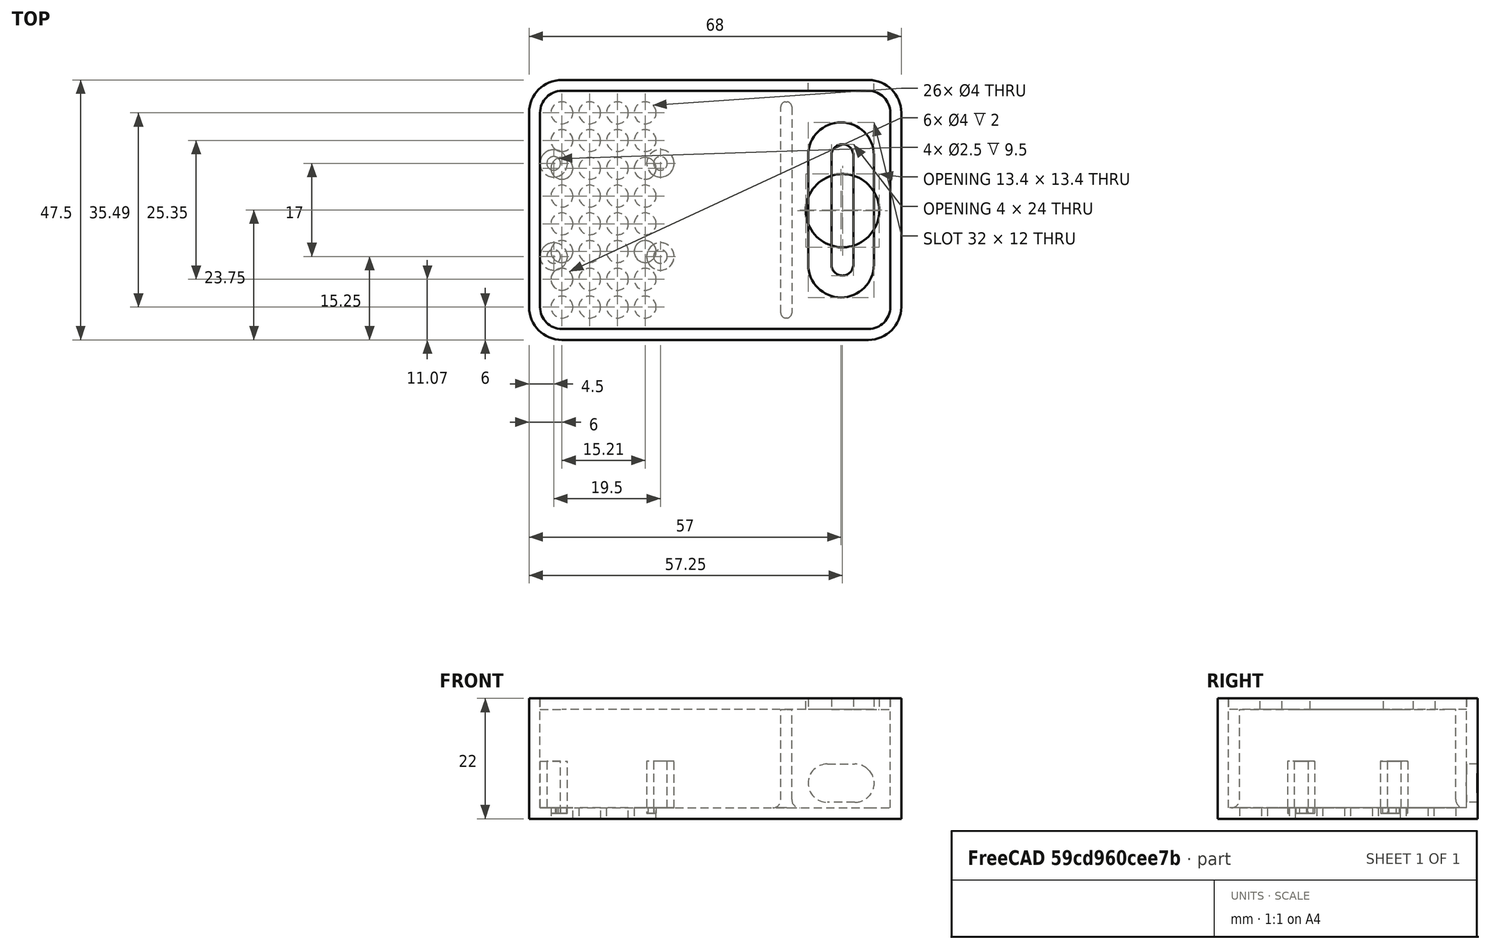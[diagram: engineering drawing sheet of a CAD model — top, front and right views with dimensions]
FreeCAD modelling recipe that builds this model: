
FCSTD DOCUMENT  (FreeCAD 0.20R29410 (Git))
Label: co2-sensor-case-v2
License: All rights reserved
LicenseURL: http://en.wikipedia.org/wiki/All_rights_reserved
objects: Sketcher::SketchObject×10, Part::Extrusion×5, PartDesign::Body×5, PartDesign::FeatureBase×4, Part::Fillet×3, PartDesign::Pocket×3, Part::Fuse×2, PartDesign::Thickness×1, Part::Cut×1
note: 38 computed .brp shape members not serialized (recipe doc carries the construction recipe); baked Part::Feature solids carry a one-line shape summary decoded from their .brp

FEATURE [Sketcher::SketchObject] Sketch
  FullyConstrained = true
  sketch-geometry (4):
    g0: LineSegment StartX=-34 StartY=23.75 StartZ=0 EndX=34 EndY=23.75 EndZ=0
    g1: LineSegment StartX=34 StartY=23.75 StartZ=0 EndX=34 EndY=-23.75 EndZ=0
    g2: LineSegment StartX=34 StartY=-23.75 StartZ=0 EndX=-34 EndY=-23.75 EndZ=0
    g3: LineSegment StartX=-34 StartY=-23.75 StartZ=0 EndX=-34 EndY=23.75 EndZ=0
  constraints (12):
    c: Coincident(g0,g1)
    c: Coincident(g1,g2)
    c: Coincident(g2,g3)
    c: Coincident(g3,g0)
    c: Horizontal(g0)
    c: Horizontal(g2)
    c: Vertical(g1)
    c: Vertical(g3)
    c: DistanceX(g0,g0) = 68
    c: DistanceY(g1,g1) = 47.5
    c: DistanceX(g-1,g0) = 34
    c: DistanceY(g-1,g0) = 23.75
FEATURE [Part::Extrusion] Extrude
  Base = -> Sketch
  Dir = (0,0,1)
  DirMode = 2
  FaceMakerClass = Part::FaceMakerBullseye
  LengthFwd = 22
  LengthRev = 0
  Solid = true
  Symmetric = false
FEATURE [Part::Fillet] Fillet
  Base = -> Extrude
  Edges = 4 edges r=6: [Edge1,Edge2,Edge5,Edge8]
FEATURE [PartDesign::FeatureBase] BaseFeature
  BaseFeature = -> Fillet
FEATURE [PartDesign::Thickness] Thickness
  Base = -> BaseFeature [Face5]
  BaseFeature = -> BaseFeature
  Intersection = false
  Join = 0
  Mode = 0
  Reversed = true
  SupportTransform = false
  Value = 2
FEATURE [Sketcher::SketchObject] Sketch001
  ExternalGeometry = -> [Thickness]
  FullyConstrained = true
  MapMode = 5
  Placement = pos=(0,0,2) rot=(0,0,1;0rad)
  Support = -> [Thickness]
  sketch-geometry (12):
    g0: Circle CenterX=-29.5 CenterY=8.5 CenterZ=0 NormalX=0 NormalY=0 NormalZ=1 AngleXU=0 Radius=2.5
    g1: Circle CenterX=-29.5 CenterY=8.5 CenterZ=0 NormalX=0 NormalY=0 NormalZ=1 AngleXU=0 Radius=1.25
    g2: Circle CenterX=-10 CenterY=8.5 CenterZ=0 NormalX=0 NormalY=0 NormalZ=1 AngleXU=0 Radius=1.25
    g3: Circle CenterX=-10 CenterY=8.5 CenterZ=0 NormalX=0 NormalY=0 NormalZ=1 AngleXU=0 Radius=2.5
    g4: Circle CenterX=-29.5 CenterY=-8.5 CenterZ=0 NormalX=0 NormalY=0 NormalZ=1 AngleXU=0 Radius=1.25
    g5: Circle CenterX=-29.5 CenterY=-8.5 CenterZ=0 NormalX=0 NormalY=0 NormalZ=1 AngleXU=0 Radius=2.5
    g6: Circle CenterX=-10 CenterY=-8.5 CenterZ=0 NormalX=0 NormalY=0 NormalZ=1 AngleXU=0 Radius=1.25
    g7: Circle CenterX=-10 CenterY=-8.5 CenterZ=0 NormalX=0 NormalY=0 NormalZ=1 AngleXU=0 Radius=2.5
    g8: LineSegment StartX=12 StartY=19.75 StartZ=0 EndX=14 EndY=19.75 EndZ=0
    g9: LineSegment StartX=14 StartY=19.75 StartZ=0 EndX=14 EndY=-19.75 EndZ=0
    g10: LineSegment StartX=14 StartY=-19.75 StartZ=0 EndX=12 EndY=-19.75 EndZ=0
    g11: LineSegment StartX=12 StartY=-19.75 StartZ=0 EndX=12 EndY=19.75 EndZ=0
  constraints (32):
    c: Coincident(g1,g0)
    c: Diameter(g0) = 5
    c: Diameter(g1) = 2.5
    c: Coincident(g2,g3)
    c: Equal(g0,g3) = 5
    c: Equal(g1,g2) = 2.5
    c: DistanceX(g0,g2) = 19.5
    c: DistanceY(g2,g0) = 0
    c: Coincident(g4,g5)
    c: Equal(g0,g5) = 5
    c: Equal(g1,g4) = 2.5
    c: Coincident(g6,g7)
    c: Equal(g5,g7) = 5
    c: Equal(g4,g6) = 2.5
    c: DistanceX(g5,g6) = 19.5
    c: DistanceY(g6,g5) = 0
    c: DistanceX(g2,g6) = 0
    c: DistanceY(g6,g2) = 17
    c: DistanceY(g-1,g2) = 8.5
    c: DistanceX(g-7,g0) = 2.5
    c: Coincident(g8,g9)
    c: Coincident(g9,g10)
    c: Coincident(g10,g11)
    c: Coincident(g11,g8)
    c: Horizontal(g8)
    c: Horizontal(g10)
    c: Vertical(g9)
    c: Vertical(g11)
    c: DistanceX(g8,g8) = 2
    c: DistanceY(g9,g9) = 39.5
    c: DistanceX(g8,g-10) = 18
    c: DistanceY(g-1,g8) = 19.75
FEATURE [Part::Extrusion] Extrude001
  Base = -> Sketch001
  Dir = (0,0,1)
  DirMode = 2
  FaceMakerClass = Part::FaceMakerBullseye
  LengthFwd = 8.5
  LengthRev = 1
  Solid = true
  Symmetric = false
FEATURE [Sketcher::SketchObject] Sketch002
  ExternalGeometry = -> [Extrude001]
  FullyConstrained = true
  MapMode = 5
  Placement = pos=(0,0,10.5) rot=(0,0,1;0rad)
  Support = -> [Extrude001]
  sketch-geometry (4):
    g0: LineSegment StartX=12 StartY=19.75 StartZ=0 EndX=14 EndY=19.75 EndZ=0
    g1: LineSegment StartX=14 StartY=19.75 StartZ=0 EndX=14 EndY=-19.75 EndZ=0
    g2: LineSegment StartX=14 StartY=-19.75 StartZ=0 EndX=12 EndY=-19.75 EndZ=0
    g3: LineSegment StartX=12 StartY=-19.75 StartZ=0 EndX=12 EndY=19.75 EndZ=0
  constraints (10):
    c: Coincident(g0,g1)
    c: Coincident(g1,g2)
    c: Coincident(g2,g3)
    c: Coincident(g3,g0)
    c: Horizontal(g0)
    c: Horizontal(g2)
    c: Vertical(g1)
    c: Vertical(g3)
    c: Coincident(g0,g-5)
    c: Coincident(g1,g-6)
FEATURE [Part::Extrusion] Extrude002
  Base = -> Sketch002
  Dir = (0,0,1)
  DirMode = 2
  FaceMakerClass = Part::FaceMakerBullseye
  LengthFwd = 9.5
  LengthRev = 0
  Solid = true
  Symmetric = false
FEATURE [Sketcher::SketchObject] Sketch003
  ExternalGeometry = -> [Thickness]
  FullyConstrained = true
  MapMode = 5
  Placement = pos=(0,0,22) rot=(0,0,1;0rad)
  Support = -> [Thickness]
  sketch-geometry (8):
    g0: LineSegment StartX=-28 StartY=21.75 StartZ=0 EndX=28 EndY=21.75 EndZ=0
    g1: LineSegment StartX=32 StartY=17.75 StartZ=0 EndX=32 EndY=-17.75 EndZ=0
    g2: LineSegment StartX=28 StartY=-21.75 StartZ=0 EndX=-28 EndY=-21.75 EndZ=0
    g3: LineSegment StartX=-32 StartY=-17.75 StartZ=0 EndX=-32 EndY=17.75 EndZ=0
    g4: ArcOfCircle CenterX=-28 CenterY=17.75 CenterZ=0 NormalX=0 NormalY=0 NormalZ=1 AngleXU=0 Radius=4 StartAngle=1.5708 EndAngle=3.14159
    g5: ArcOfCircle CenterX=-28 CenterY=-17.75 CenterZ=0 NormalX=0 NormalY=0 NormalZ=1 AngleXU=0 Radius=4 StartAngle=3.14159 EndAngle=4.71239
    g6: ArcOfCircle CenterX=28 CenterY=-17.75 CenterZ=0 NormalX=0 NormalY=0 NormalZ=1 AngleXU=0 Radius=4 StartAngle=4.71239 EndAngle=6.28319
    g7: ArcOfCircle CenterX=28 CenterY=17.75 CenterZ=0 NormalX=0 NormalY=0 NormalZ=1 AngleXU=0 Radius=4 StartAngle=-9e-16 EndAngle=1.5708
  constraints (20):
    c: Coincident(g0,g-4)
    c: Coincident(g0,g-10)
    c: Coincident(g1,g-10)
    c: Coincident(g1,g-9)
    c: Coincident(g2,g-8)
    c: Coincident(g2,g-7)
    c: Coincident(g3,g-6)
    c: Coincident(g3,g-5)
    c: Coincident(g4,g-3)
    c: Coincident(g4,g0)
    c: Coincident(g4,g3)
    c: Coincident(g5,g-6)
    c: Coincident(g5,g3)
    c: Coincident(g5,g2)
    c: Coincident(g6,g-8)
    c: Coincident(g6,g2)
    c: Coincident(g6,g1)
    c: Coincident(g7,g-10)
    c: Coincident(g7,g0)
    c: Coincident(g7,g1)
FEATURE [Part::Extrusion] Extrude003
  Base = -> Sketch003
  Dir = (0,0,1)
  DirMode = 2
  FaceMakerClass = Part::FaceMakerBullseye
  LengthFwd = 2
  LengthRev = 0
  Reversed = true
  Solid = true
  Symmetric = false
FEATURE [Sketcher::SketchObject] Sketch004
  ExternalGeometry = -> [Thickness]
  FullyConstrained = false
  MapMode = 5
  Placement = pos=(0,0,22) rot=(0,0,1;0rad)
  Support = -> [Extrude003]
  sketch-geometry (5):
    g0: ArcOfCircle CenterX=23.25 CenterY=10 CenterZ=0 NormalX=0 NormalY=0 NormalZ=1 AngleXU=0 Radius=2 StartAngle=4e-16 EndAngle=3.14159
    g1: ArcOfCircle CenterX=23.25 CenterY=-10 CenterZ=0 NormalX=0 NormalY=0 NormalZ=1 AngleXU=0 Radius=2 StartAngle=3.14159 EndAngle=6.28319
    g2: LineSegment StartX=21.25 StartY=10 StartZ=0 EndX=21.25 EndY=-10 EndZ=0
    g3: LineSegment StartX=25.25 StartY=-10 StartZ=0 EndX=25.25 EndY=10 EndZ=0
    g4: Circle CenterX=23.2654 CenterY=-0.133764 CenterZ=0 NormalX=0 NormalY=0 NormalZ=1 AngleXU=0 Radius=6.6979
  constraints (9):
    c: Tangent(g0,g2) = -1.5708
    c: Tangent(g2,g1) = -1.5708
    c: Tangent(g1,g3) = -1.5708
    c: Tangent(g3,g0) = -1.5708
    c: Equal(g0,g1)
    c: Symmetric(g0,g1,g-1)
    c: DistanceY(g-1,g0) = 10
    c: Radius(g0) = 2
    c: DistanceX(g0,g-3) = 6.75
FEATURE [PartDesign::FeatureBase] BaseFeature001
  BaseFeature = -> Extrude003
FEATURE [PartDesign::Pocket] Pocket
  BaseFeature = -> BaseFeature001
  Direction = (0,0,-1)
  Length = 2
  Length2 = 5
  Profile = -> Sketch004
  ReferenceAxis = -> Sketch004 [N_Axis]
  Type = 0
FEATURE [Sketcher::SketchObject] Sketch005
  ExternalGeometry = -> [Thickness]
  FullyConstrained = true
  MapMode = 5
  Placement = pos=(0,0,0) rot=(1,0,0;3.14159rad)
  Support = -> [Thickness]
  sketch-geometry (63):
    g0: Circle CenterX=-28 CenterY=17.75 CenterZ=0 NormalX=0 NormalY=0 NormalZ=1 AngleXU=0 Radius=2
    g1: Circle CenterX=-22.93 CenterY=17.75 CenterZ=0 NormalX=0 NormalY=0 NormalZ=1 AngleXU=0 Radius=2
    g2: LineSegment StartX=-28 StartY=17.75 StartZ=0 EndX=-22.93 EndY=17.75 EndZ=0
    g3: Circle CenterX=-17.86 CenterY=17.75 CenterZ=0 NormalX=0 NormalY=0 NormalZ=1 AngleXU=0 Radius=2
    g4: LineSegment StartX=-22.93 StartY=17.75 StartZ=0 EndX=-17.86 EndY=17.75 EndZ=0
    g5: Circle CenterX=-12.79 CenterY=17.75 CenterZ=0 NormalX=0 NormalY=0 NormalZ=1 AngleXU=0 Radius=2
    g6: LineSegment StartX=-17.86 StartY=17.75 StartZ=0 EndX=-12.79 EndY=17.75 EndZ=0
    g7: Circle CenterX=-28 CenterY=12.68 CenterZ=0 NormalX=0 NormalY=0 NormalZ=1 AngleXU=0 Radius=2
    g8: LineSegment StartX=-28 StartY=17.75 StartZ=0 EndX=-28 EndY=12.68 EndZ=0
    g9: Circle CenterX=-22.93 CenterY=12.68 CenterZ=0 NormalX=0 NormalY=0 NormalZ=1 AngleXU=0 Radius=2
    g10: LineSegment StartX=-28 StartY=12.68 StartZ=0 EndX=-22.93 EndY=12.68 EndZ=0
    g11: Circle CenterX=-17.86 CenterY=12.68 CenterZ=0 NormalX=0 NormalY=0 NormalZ=1 AngleXU=0 Radius=2
    g12: LineSegment StartX=-22.93 StartY=12.68 StartZ=0 EndX=-17.86 EndY=12.68 EndZ=0
    g13: Circle CenterX=-12.79 CenterY=12.68 CenterZ=0 NormalX=0 NormalY=0 NormalZ=1 AngleXU=0 Radius=2
    g14: LineSegment StartX=-17.86 StartY=12.68 StartZ=0 EndX=-12.79 EndY=12.68 EndZ=0
    g15: Circle CenterX=-28 CenterY=7.61 CenterZ=0 NormalX=0 NormalY=0 NormalZ=1 AngleXU=0 Radius=2
    g16: LineSegment StartX=-28 StartY=12.68 StartZ=0 EndX=-28 EndY=7.61 EndZ=0
    g17: Circle CenterX=-22.93 CenterY=7.61 CenterZ=0 NormalX=0 NormalY=0 NormalZ=1 AngleXU=0 Radius=2
    g18: LineSegment StartX=-28 StartY=7.61 StartZ=0 EndX=-22.93 EndY=7.61 EndZ=0
    g19: Circle CenterX=-17.86 CenterY=7.61 CenterZ=0 NormalX=0 NormalY=0 NormalZ=1 AngleXU=0 Radius=2
    g20: LineSegment StartX=-22.93 StartY=7.61 StartZ=0 EndX=-17.86 EndY=7.61 EndZ=0
    g21: Circle CenterX=-12.79 CenterY=7.61 CenterZ=0 NormalX=0 NormalY=0 NormalZ=1 AngleXU=0 Radius=2
    g22: LineSegment StartX=-17.86 StartY=7.61 StartZ=0 EndX=-12.79 EndY=7.61 EndZ=0
    g23: Circle CenterX=-28 CenterY=2.54 CenterZ=0 NormalX=0 NormalY=0 NormalZ=1 AngleXU=0 Radius=2
    g24: LineSegment StartX=-28 StartY=7.61 StartZ=0 EndX=-28 EndY=2.54 EndZ=0
    g25: Circle CenterX=-22.93 CenterY=2.54 CenterZ=0 NormalX=0 NormalY=0 NormalZ=1 AngleXU=0 Radius=2
    g26: LineSegment StartX=-28 StartY=2.54 StartZ=0 EndX=-22.93 EndY=2.54 EndZ=0
    g27: Circle CenterX=-17.86 CenterY=2.54 CenterZ=0 NormalX=0 NormalY=0 NormalZ=1 AngleXU=0 Radius=2
    g28: LineSegment StartX=-22.93 StartY=2.54 StartZ=0 EndX=-17.86 EndY=2.54 EndZ=0
    g29: Circle CenterX=-12.79 CenterY=2.54 CenterZ=0 NormalX=0 NormalY=0 NormalZ=1 AngleXU=0 Radius=2
    g30: LineSegment StartX=-17.86 StartY=2.54 StartZ=0 EndX=-12.79 EndY=2.54 EndZ=0
    g31: Circle CenterX=-28 CenterY=-2.53 CenterZ=0 NormalX=0 NormalY=0 NormalZ=1 AngleXU=0 Radius=2
    g32: LineSegment StartX=-28 StartY=2.54 StartZ=0 EndX=-28 EndY=-2.53 EndZ=0
    g33: Circle CenterX=-22.93 CenterY=-2.53 CenterZ=0 NormalX=0 NormalY=0 NormalZ=1 AngleXU=0 Radius=2
    g34: LineSegment StartX=-28 StartY=-2.53 StartZ=0 EndX=-22.93 EndY=-2.53 EndZ=0
    g35: Circle CenterX=-17.86 CenterY=-2.53 CenterZ=0 NormalX=0 NormalY=0 NormalZ=1 AngleXU=0 Radius=2
    g36: LineSegment StartX=-22.93 StartY=-2.53 StartZ=0 EndX=-17.86 EndY=-2.53 EndZ=0
    g37: Circle CenterX=-12.79 CenterY=-2.53 CenterZ=0 NormalX=0 NormalY=0 NormalZ=1 AngleXU=0 Radius=2
    g38: LineSegment StartX=-17.86 StartY=-2.53 StartZ=0 EndX=-12.79 EndY=-2.53 EndZ=0
    g39: Circle CenterX=-28 CenterY=-7.6 CenterZ=0 NormalX=0 NormalY=0 NormalZ=1 AngleXU=0 Radius=2
    g40: LineSegment StartX=-28 StartY=-2.53 StartZ=0 EndX=-28 EndY=-7.6 EndZ=0
    g41: Circle CenterX=-22.93 CenterY=-7.6 CenterZ=0 NormalX=0 NormalY=0 NormalZ=1 AngleXU=0 Radius=2
    g42: LineSegment StartX=-28 StartY=-7.6 StartZ=0 EndX=-22.93 EndY=-7.6 EndZ=0
    g43: Circle CenterX=-17.86 CenterY=-7.6 CenterZ=0 NormalX=0 NormalY=0 NormalZ=1 AngleXU=0 Radius=2
    g44: LineSegment StartX=-22.93 StartY=-7.6 StartZ=0 EndX=-17.86 EndY=-7.6 EndZ=0
    g45: Circle CenterX=-12.79 CenterY=-7.6 CenterZ=0 NormalX=0 NormalY=0 NormalZ=1 AngleXU=0 Radius=2
    g46: LineSegment StartX=-17.86 StartY=-7.6 StartZ=0 EndX=-12.79 EndY=-7.6 EndZ=0
    g47: Circle CenterX=-28 CenterY=-12.67 CenterZ=0 NormalX=0 NormalY=0 NormalZ=1 AngleXU=0 Radius=2
    g48: LineSegment StartX=-28 StartY=-7.6 StartZ=0 EndX=-28 EndY=-12.67 EndZ=0
    g49: Circle CenterX=-22.93 CenterY=-12.67 CenterZ=0 NormalX=0 NormalY=0 NormalZ=1 AngleXU=0 Radius=2
    g50: LineSegment StartX=-28 StartY=-12.67 StartZ=0 EndX=-22.93 EndY=-12.67 EndZ=0
    g51: Circle CenterX=-17.86 CenterY=-12.67 CenterZ=0 NormalX=0 NormalY=0 NormalZ=1 AngleXU=0 Radius=2
    g52: LineSegment StartX=-22.93 StartY=-12.67 StartZ=0 EndX=-17.86 EndY=-12.67 EndZ=0
    g53: Circle CenterX=-12.79 CenterY=-12.67 CenterZ=0 NormalX=0 NormalY=0 NormalZ=1 AngleXU=0 Radius=2
    g54: LineSegment StartX=-17.86 StartY=-12.67 StartZ=0 EndX=-12.79 EndY=-12.67 EndZ=0
    g55: Circle CenterX=-28 CenterY=-17.74 CenterZ=0 NormalX=0 NormalY=0 NormalZ=1 AngleXU=0 Radius=2
    g56: LineSegment StartX=-28 StartY=-12.67 StartZ=0 EndX=-28 EndY=-17.74 EndZ=0
    g57: Circle CenterX=-22.93 CenterY=-17.74 CenterZ=0 NormalX=0 NormalY=0 NormalZ=1 AngleXU=0 Radius=2
    g58: LineSegment StartX=-28 StartY=-17.74 StartZ=0 EndX=-22.93 EndY=-17.74 EndZ=0
    g59: Circle CenterX=-17.86 CenterY=-17.74 CenterZ=0 NormalX=0 NormalY=0 NormalZ=1 AngleXU=0 Radius=2
    g60: LineSegment StartX=-22.93 StartY=-17.74 StartZ=0 EndX=-17.86 EndY=-17.74 EndZ=0
    g61: Circle CenterX=-12.79 CenterY=-17.74 CenterZ=0 NormalX=0 NormalY=0 NormalZ=1 AngleXU=0 Radius=2
    g62: LineSegment StartX=-17.86 StartY=-17.74 StartZ=0 EndX=-12.79 EndY=-17.74 EndZ=0
  constraints (157):
    c: Coincident(g0,g-6)
    c: Radius(g0) = 2
    c: Equal(g0,g1) = 2
    c: Coincident(g0,g2)
    c: Coincident(g1,g2)
    c: Distance(g2) = 5.07
    c: Angle(g2) = 0
    c: Equal(g0,g3) = 2
    c: Coincident(g1,g4)
    c: Coincident(g3,g4)
    c: Equal(g2,g4)
    c: Parallel(g4,g2)
    c: Equal(g0,g5) = 2
    c: Coincident(g3,g6)
    c: Coincident(g5,g6)
    c: Equal(g2,g6)
    c: Parallel(g6,g2)
    c: Equal(g0,g7) = 2
    c: Coincident(g0,g8)
    c: Coincident(g7,g8)
    c: Equal(g8,g2)
    c: Perpendicular(g8,g2)
    c: Equal(g0,g9) = 2
    c: Coincident(g7,g10)
    c: Coincident(g9,g10)
    c: Equal(g2,g10)
    c: Parallel(g10,g2)
    c: Equal(g0,g11) = 2
    c: Coincident(g9,g12)
    c: Coincident(g11,g12)
    c: Equal(g2,g12)
    c: Parallel(g12,g2)
    c: Equal(g0,g13) = 2
    c: Coincident(g11,g14)
    c: Coincident(g13,g14)
    c: Equal(g2,g14)
    c: Parallel(g14,g2)
    c: Equal(g0,g15) = 2
    c: Coincident(g7,g16)
    c: Coincident(g15,g16)
    c: Equal(g8,g16)
    c: Perpendicular(g16,g2)
    c: Equal(g0,g17) = 2
    c: Coincident(g15,g18)
    c: Coincident(g17,g18)
    c: Equal(g2,g18)
    c: Parallel(g18,g2)
    c: Equal(g0,g19) = 2
    c: Coincident(g17,g20)
    c: Coincident(g19,g20)
    c: Equal(g2,g20)
    c: Parallel(g20,g2)
    c: Equal(g0,g21) = 2
    c: Coincident(g19,g22)
    c: Coincident(g21,g22)
    c: Equal(g2,g22)
    c: Parallel(g22,g2)
    c: Equal(g0,g23) = 2
    c: Coincident(g15,g24)
    c: Coincident(g23,g24)
    c: Equal(g8,g24)
    c: Perpendicular(g24,g2)
    c: Equal(g0,g25) = 2
    c: Coincident(g23,g26)
    c: Coincident(g25,g26)
    c: Equal(g2,g26)
    c: Parallel(g26,g2)
    c: Equal(g0,g27) = 2
    c: Coincident(g25,g28)
    c: Coincident(g27,g28)
    c: Equal(g2,g28)
    c: Parallel(g28,g2)
    c: Equal(g0,g29) = 2
    c: Coincident(g27,g30)
    c: Coincident(g29,g30)
    c: Equal(g2,g30)
    c: Parallel(g30,g2)
    c: Equal(g0,g31) = 2
    c: Coincident(g23,g32)
    c: Coincident(g31,g32)
    c: Equal(g8,g32)
    c: Perpendicular(g32,g2)
    c: Equal(g0,g33) = 2
    c: Coincident(g31,g34)
    c: Coincident(g33,g34)
    c: Equal(g2,g34)
    c: Parallel(g34,g2)
    c: Equal(g0,g35) = 2
    c: Coincident(g33,g36)
    c: Coincident(g35,g36)
    c: Equal(g2,g36)
    c: Parallel(g36,g2)
    c: Equal(g0,g37) = 2
    c: Coincident(g35,g38)
    c: Coincident(g37,g38)
    c: Equal(g2,g38)
    c: Parallel(g38,g2)
    c: Equal(g0,g39) = 2
    c: Coincident(g31,g40)
    c: Coincident(g39,g40)
    c: Equal(g8,g40)
    c: Perpendicular(g40,g2)
    c: Equal(g0,g41) = 2
    c: Coincident(g39,g42)
    c: Coincident(g41,g42)
    c: Equal(g2,g42)
    c: Parallel(g42,g2)
    c: Equal(g0,g43) = 2
    c: Coincident(g41,g44)
    c: Coincident(g43,g44)
    c: Equal(g2,g44)
    c: Parallel(g44,g2)
    c: Equal(g0,g45) = 2
    c: Coincident(g43,g46)
    c: Coincident(g45,g46)
    c: Equal(g2,g46)
    c: Parallel(g46,g2)
    c: Equal(g0,g47) = 2
    c: Coincident(g39,g48)
    c: Coincident(g47,g48)
    c: Equal(g8,g48)
    c: Perpendicular(g48,g2)
    c: Equal(g0,g49) = 2
    c: Coincident(g47,g50)
    c: Coincident(g49,g50)
    c: Equal(g2,g50)
    c: Parallel(g50,g2)
    c: Equal(g0,g51) = 2
    c: Coincident(g49,g52)
    c: Coincident(g51,g52)
    c: Equal(g2,g52)
    c: Parallel(g52,g2)
    c: Equal(g0,g53) = 2
    c: Coincident(g51,g54)
    c: Coincident(g53,g54)
    c: Equal(g2,g54)
    c: Parallel(g54,g2)
    c: Equal(g0,g55) = 2
    c: Coincident(g47,g56)
    c: Coincident(g55,g56)
    c: Equal(g8,g56)
    c: Perpendicular(g56,g2)
    c: Equal(g0,g57) = 2
    c: Coincident(g55,g58)
    c: Coincident(g57,g58)
    c: Equal(g2,g58)
    c: Parallel(g58,g2)
    c: Equal(g0,g59) = 2
    c: Coincident(g57,g60)
    c: Coincident(g59,g60)
    c: Equal(g2,g60)
    c: Parallel(g60,g2)
    c: Equal(g0,g61) = 2
    c: Coincident(g59,g62)
    c: Coincident(g61,g62)
    c: Equal(g2,g62)
    c: Parallel(g62,g2)
FEATURE [PartDesign::Body] Body
  BaseFeature = -> Fillet
  Group = -> [BaseFeature,Thickness,Sketch005]
  Origin = -> Origin
  Tip = -> Thickness
FEATURE [PartDesign::Body] Body002
  Origin = -> Origin002
FEATURE [Part::Extrusion] Extrude004
  Base = -> Sketch005
  Dir = (0,0,-1)
  DirMode = 2
  FaceMakerClass = Part::FaceMakerBullseye
  LengthFwd = -2
  LengthRev = 0
  Solid = true
  Symmetric = false
FEATURE [Part::Cut] Cut
  Base = -> Body
  Tool = -> Extrude004
FEATURE [Part::Fuse] Fusion
  Base = -> Extrude001
  Tool = -> Extrude002
FEATURE [Part::Fuse] Fusion001
  Base = -> Cut
  Tool = -> Fusion
FEATURE [Part::Fillet] Fillet001
  Base = -> Fusion001
  Edges = 8 edges r=0.9: [Edge241,Edge243,Edge245,Edge247,Edge249,Edge250,Edge252,Edge254]
FEATURE [Part::Fillet] Fillet002
  Base = -> Fillet001
  Edges = 7 edges r=1.5: [Edge2,Edge3,Edge4,Edge5,Edge6,Edge7,Edge8]
FEATURE [Sketcher::SketchObject] Sketch006
  ExternalGeometry = -> [Fillet002]
  FullyConstrained = true
  MapMode = 5
  Placement = pos=(0,23.75,0) rot=(0,0.707107,0.707107;3.14159rad)
  Support = -> [Fillet002]
  sketch-geometry (4):
    g0: ArcOfCircle CenterX=-25.5 CenterY=6.5 CenterZ=0 NormalX=0 NormalY=0 NormalZ=1 AngleXU=0 Radius=3.5 StartAngle=1.5708 EndAngle=4.71239
    g1: ArcOfCircle CenterX=-20.5 CenterY=6.5 CenterZ=0 NormalX=0 NormalY=0 NormalZ=1 AngleXU=0 Radius=3.5 StartAngle=4.71239 EndAngle=7.85398
    g2: LineSegment StartX=-25.5 StartY=3 StartZ=0 EndX=-20.5 EndY=3 EndZ=0
    g3: LineSegment StartX=-20.5 StartY=10 StartZ=0 EndX=-25.5 EndY=10 EndZ=0
  constraints (10):
    c: Tangent(g0,g2) = -1.5708
    c: Tangent(g2,g1) = -1.5708
    c: Tangent(g1,g3) = -1.5708
    c: Tangent(g3,g0) = -1.5708
    c: Equal(g0,g1)
    c: Horizontal(g2)
    c: DistanceY(g1,g1) = 7
    c: DistanceX(g0,g1) = 5
    c: DistanceY(g1,g-6) = 10
    c: DistanceX(g1,g-6) = 6.5
FEATURE [PartDesign::FeatureBase] BaseFeature002
  BaseFeature = -> Fillet002
FEATURE [PartDesign::Pocket] Pocket001
  BaseFeature = -> BaseFeature002
  Direction = (0,-1,2e-16)
  Length = 5
  Length2 = 5
  Profile = -> Sketch006
  ReferenceAxis = -> Sketch006 [N_Axis]
  Type = 0
FEATURE [PartDesign::Body] Body003
  BaseFeature = -> Fillet002
  Group = -> [BaseFeature002,Sketch006,Pocket001]
  Origin = -> Origin003
  Tip = -> Pocket001
FEATURE [Sketcher::SketchObject] Sketch007
  ExternalGeometry = -> [Pocket]
  FullyConstrained = true
  MapMode = 5
  Placement = pos=(0,0,22) rot=(0,0,1;0rad)
  Support = -> [Pocket]
  sketch-geometry (1):
    g0: Circle CenterX=23.2654 CenterY=0 CenterZ=0 NormalX=0 NormalY=0 NormalZ=1 AngleXU=0 Radius=6.75
  constraints (3):
    c: PointOnObject(g0,g-1)
    c: Diameter(g0) = 13.5
    c: DistanceX(g-5,g0) = 0
FEATURE [PartDesign::Body] Body001
  BaseFeature = -> Extrude003
  Group = -> [BaseFeature001,Sketch004,Pocket,Sketch007]
  Origin = -> Origin001
  Tip = -> Pocket
FEATURE [Sketcher::SketchObject] Sketch008
  FullyConstrained = true
  Placement = pos=(0,0,22) rot=(0,0,1;0rad)
  sketch-geometry (4):
    g0: ArcOfCircle CenterX=23 CenterY=10 CenterZ=0 NormalX=0 NormalY=0 NormalZ=1 AngleXU=0 Radius=6 StartAngle=0 EndAngle=3.14159
    g1: ArcOfCircle CenterX=23 CenterY=-10 CenterZ=0 NormalX=0 NormalY=0 NormalZ=1 AngleXU=0 Radius=6 StartAngle=3.14159 EndAngle=6.28319
    g2: LineSegment StartX=17 StartY=10 StartZ=0 EndX=17 EndY=-10 EndZ=0
    g3: LineSegment StartX=29 StartY=-10 StartZ=0 EndX=29 EndY=10 EndZ=0
  constraints (9):
    c: Tangent(g0,g2) = -1.5708
    c: Tangent(g2,g1) = -1.5708
    c: Tangent(g1,g3) = -1.5708
    c: Tangent(g3,g0) = -1.5708
    c: Equal(g0,g1)
    c: Symmetric(g0,g1,g-1)
    c: DistanceY(g-1,g0) = 10
    c: Radius(g0) = 6
    c: DistanceX(g-1,g0) = 23
FEATURE [PartDesign::FeatureBase] BaseFeature003
  BaseFeature = -> Extrude003
FEATURE [PartDesign::Pocket] Pocket002
  BaseFeature = -> BaseFeature003
  Direction = (0,0,-1)
  Length = 3
  Length2 = 5
  Profile = -> Sketch008
  ReferenceAxis = -> Sketch008 [N_Axis]
  Type = 0
FEATURE [Sketcher::SketchObject] Sketch009
  FullyConstrained = true
  MapMode = 5
  Placement = pos=(0,0,22) rot=(0,0,1;0rad)
  Support = -> [Pocket002]
  sketch-geometry (1):
    g0: Circle CenterX=23.5 CenterY=0 CenterZ=0 NormalX=0 NormalY=0 NormalZ=1 AngleXU=0 Radius=6.75
  constraints (3):
    c: PointOnObject(g0,g-1)
    c: Diameter(g0) = 13.5
    c: DistanceX(g-1,g0) = 23.5
FEATURE [PartDesign::Body] Body004
  BaseFeature = -> Extrude003
  Group = -> [BaseFeature003,Sketch008,Pocket002,Sketch009]
  Origin = -> Origin004
  Tip = -> Pocket002
